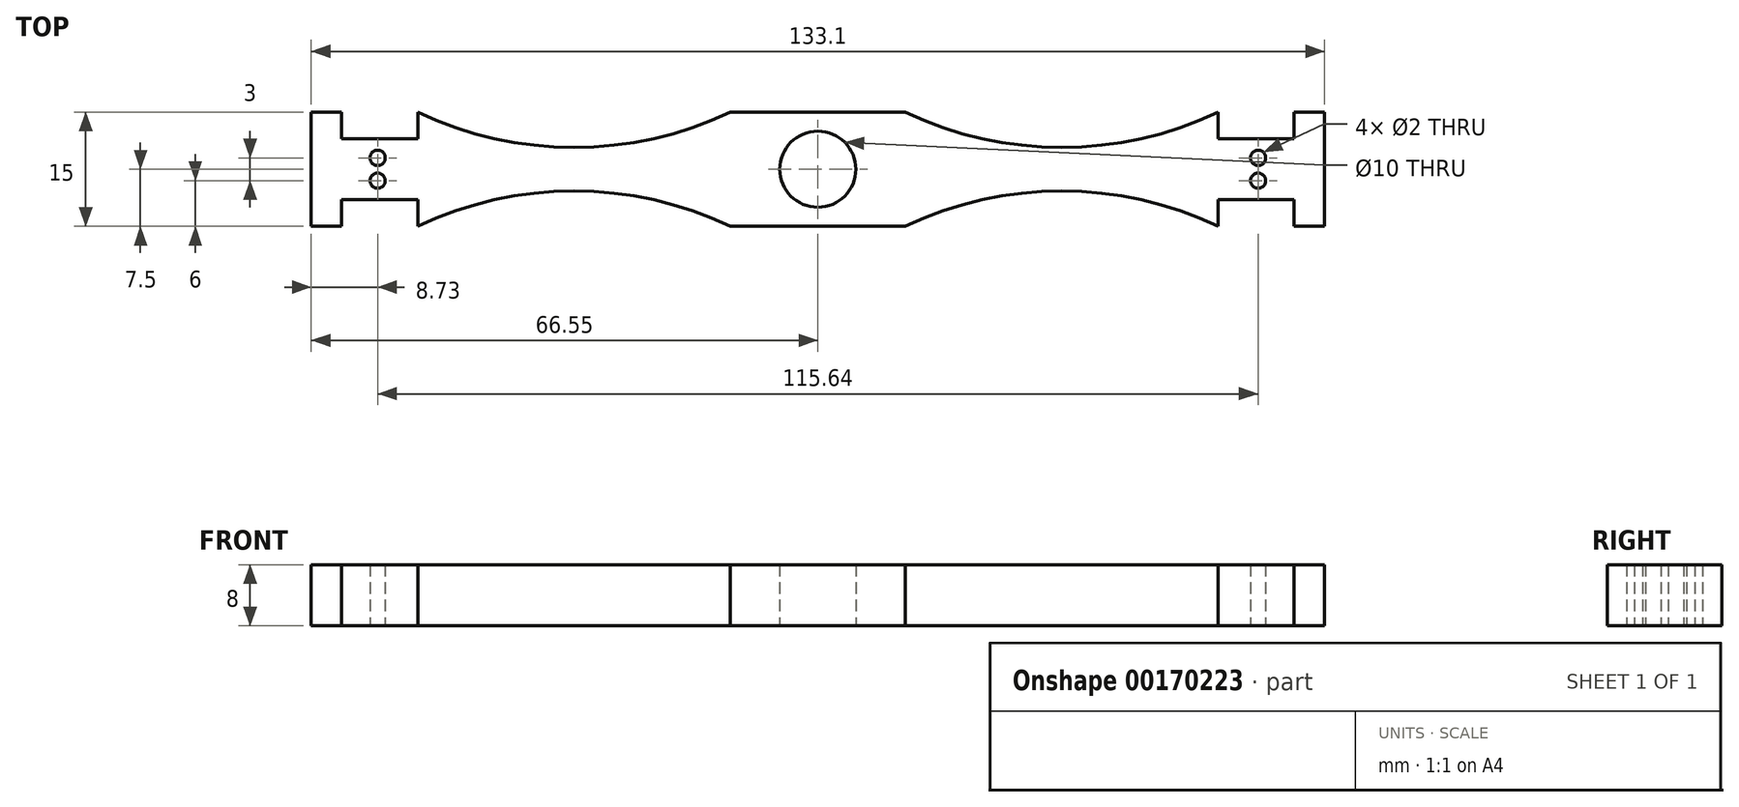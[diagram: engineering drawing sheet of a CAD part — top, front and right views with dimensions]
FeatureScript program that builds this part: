
annotation { "Feature Type Name" : "Feature", "Feature Type Description" : "" }
export const myFeature = defineFeature(function(context is Context, id is Id, definition is map)
    precondition{}
    {
        {
            var Q0;
            Q0=qCreatedBy(makeId("Top.planeOp"),FACE);
            var sketch = newSketch(context, id + "F0", { "sketchPlane" : qUnion([Q0])});
            skLineSegment(sketch, "E0.bottom", {"start": v(-11.5, 7.5) * mm, "end": v(11.5, 7.5) * mm});
            skLineSegment(sketch, "E0.top", {"start": v(-11.5, -7.5) * mm, "end": v(11.5, -7.5) * mm});
            skLineSegment(sketch, "E0.left", {"start": v(-11.5, 7.5) * mm, "end": v(-11.5, -7.5) * mm});
            skLineSegment(sketch, "E0.right", {"start": v(11.5, 7.5) * mm, "end": v(11.5, -7.5) * mm});
            skPoint(sketch, "E0.middle", {"position": v(0, 0) * mm});
            skArc(sketch, "E1", {"start": v(-52.55, 7.5) * mm, "mid": v(-32.02, 2.86) * mm, "end": v(-11.5, 7.5) * mm});
            skLineSegment(sketch, "E2", {"start": v(-52.55, 7.5) * mm, "end": v(-52.55, 4) * mm});
            skLineSegment(sketch, "E3", {"start": v(-52.55, 4) * mm, "end": v(-62.55, 4) * mm});
            skLineSegment(sketch, "E4", {"start": v(-62.55, 4) * mm, "end": v(-62.55, 7.5) * mm});
            skLineSegment(sketch, "E5", {"start": v(-62.55, 7.5) * mm, "end": v(-66.55, 7.5) * mm});
            skArc(sketch, "E6.MirrorCS", {"start": v(-52.55, -7.5) * mm, "mid": v(-32.02, -2.86) * mm, "end": v(-11.5, -7.5) * mm});
            skLineSegment(sketch, "E7.MirrorCS", {"start": v(-52.55, -4) * mm, "end": v(-62.55, -4) * mm});
            skLineSegment(sketch, "E8.MirrorCS", {"start": v(-62.55, -7.5) * mm, "end": v(-66.55, -7.5) * mm});
            skLineSegment(sketch, "E9.MirrorCS", {"start": v(-62.55, -4) * mm, "end": v(-62.55, -7.5) * mm});
            skLineSegment(sketch, "E10.MirrorCS", {"start": v(-52.55, -7.5) * mm, "end": v(-52.55, -4) * mm});
            skLineSegment(sketch, "E11", {"start": v(-66.55, 7.5) * mm, "end": v(-66.55, -7.5) * mm});
            skPoint(sketch, "E12", {"position": v(-57.82, 1.5) * mm});
            skPoint(sketch, "E13", {"position": v(-57.82, -1.5) * mm});
            skArc(sketch, "E14.MirrorCS", {"start": v(52.55, 7.5) * mm, "mid": v(32.02, 2.86) * mm, "end": v(11.5, 7.5) * mm});
            skArc(sketch, "E15.MirrorCS", {"start": v(52.55, -7.5) * mm, "mid": v(32.02, -2.86) * mm, "end": v(11.5, -7.5) * mm});
            skLineSegment(sketch, "E16.MirrorCS", {"start": v(52.55, 7.5) * mm, "end": v(52.55, 4) * mm});
            skLineSegment(sketch, "E17.MirrorCS", {"start": v(52.55, -7.5) * mm, "end": v(52.55, -4) * mm});
            skLineSegment(sketch, "E18.MirrorCS", {"start": v(52.55, -4) * mm, "end": v(62.55, -4) * mm});
            skLineSegment(sketch, "E19.MirrorCS", {"start": v(52.55, 4) * mm, "end": v(62.55, 4) * mm});
            skLineSegment(sketch, "E20.MirrorCS", {"start": v(62.55, 4) * mm, "end": v(62.55, 7.5) * mm});
            skLineSegment(sketch, "E21.MirrorCS", {"start": v(62.55, 7.5) * mm, "end": v(66.55, 7.5) * mm});
            skLineSegment(sketch, "E22.MirrorCS", {"start": v(66.55, 7.5) * mm, "end": v(66.55, -7.5) * mm});
            skLineSegment(sketch, "E23.MirrorCS", {"start": v(62.55, -7.5) * mm, "end": v(66.55, -7.5) * mm});
            skLineSegment(sketch, "E24.MirrorCS", {"start": v(62.55, -4) * mm, "end": v(62.55, -7.5) * mm});
            skPoint(sketch, "E25.MirrorP", {"position": v(57.82, -1.5) * mm});
            skPoint(sketch, "E26.MirrorP", {"position": v(57.82, 1.5) * mm});
            skSolve(sketch);
        }
        {
            var Q0;
            Q0 = qSketchRegion(id + "F0", true);
            extrude(context, id + "F1", {"entities" : qUnion([Q0]), "depth" : 8 * mm});
        }
        {
            var Q0;
            Q0=sQuery(id+"F0.wireOp",VERTEX,"E12");
            var Q1;
            Q1=sQuery(id+"F0.wireOp",VERTEX,"E13");
            var Q2;
            Q2=sQuery(id+"F0.wireOp",VERTEX,"E26.MirrorP");
            var Q3;
            Q3=sQuery(id+"F0.wireOp",VERTEX,"E25.MirrorP");
            var Q4;
            Q4=makeQuery(id+"F1.opExtrude","SWEPT_BODY",BODY,{"disambiguationData":[OSD([sQuery(id+"F0.wireOp",EDGE,"E0.bottom"),sQuery(id+"F0.wireOp",EDGE,"E0.top"),sQuery(id+"F0.wireOp",EDGE,"E1"),sQuery(id+"F0.wireOp",EDGE,"E2"),sQuery(id+"F0.wireOp",EDGE,"E3"),sQuery(id+"F0.wireOp",EDGE,"E4"),sQuery(id+"F0.wireOp",EDGE,"E5"),sQuery(id+"F0.wireOp",EDGE,"E6.MirrorCS"),sQuery(id+"F0.wireOp",EDGE,"E7.MirrorCS"),sQuery(id+"F0.wireOp",EDGE,"E8.MirrorCS"),sQuery(id+"F0.wireOp",EDGE,"E9.MirrorCS"),sQuery(id+"F0.wireOp",EDGE,"E10.MirrorCS"),sQuery(id+"F0.wireOp",EDGE,"E11"),sQuery(id+"F0.wireOp",EDGE,"E14.MirrorCS"),sQuery(id+"F0.wireOp",EDGE,"E15.MirrorCS"),sQuery(id+"F0.wireOp",EDGE,"E16.MirrorCS"),sQuery(id+"F0.wireOp",EDGE,"E17.MirrorCS"),sQuery(id+"F0.wireOp",EDGE,"E19.MirrorCS"),sQuery(id+"F0.wireOp",EDGE,"E20.MirrorCS"),sQuery(id+"F0.wireOp",EDGE,"E21.MirrorCS"),sQuery(id+"F0.wireOp",EDGE,"E22.MirrorCS"),sQuery(id+"F0.wireOp",EDGE,"E23.MirrorCS"),sQuery(id+"F0.wireOp",EDGE,"E24.MirrorCS"),sQuery(id+"F0.wireOp",EDGE,"E18.MirrorCS")])]});
            hole(context, id + "F2", {"style" : HoleStyle.SIMPLE, "endStyle" : HoleEndStyle.BLIND, "oppositeDirection" : true, "holeDiameter" : 2 * mm, "holeDepth" : 50 * mm, "startFromSketch" : true, "locations" : qUnion([Q0, Q1, Q2, Q3]), "scope" : qUnion([Q4])});
        }
        {
            var Q0;
            Q0=sQuery(id+"F0.wireOp",VERTEX,"E0.middle");
            var Q1;
            Q1=makeQuery(id+"F1.opExtrude","SWEPT_BODY",BODY,{"disambiguationData":[OSD([sQuery(id+"F0.wireOp",EDGE,"E0.bottom"),sQuery(id+"F0.wireOp",EDGE,"E0.top"),sQuery(id+"F0.wireOp",EDGE,"E1"),sQuery(id+"F0.wireOp",EDGE,"E2"),sQuery(id+"F0.wireOp",EDGE,"E3"),sQuery(id+"F0.wireOp",EDGE,"E4"),sQuery(id+"F0.wireOp",EDGE,"E5"),sQuery(id+"F0.wireOp",EDGE,"E6.MirrorCS"),sQuery(id+"F0.wireOp",EDGE,"E7.MirrorCS"),sQuery(id+"F0.wireOp",EDGE,"E8.MirrorCS"),sQuery(id+"F0.wireOp",EDGE,"E9.MirrorCS"),sQuery(id+"F0.wireOp",EDGE,"E10.MirrorCS"),sQuery(id+"F0.wireOp",EDGE,"E11"),sQuery(id+"F0.wireOp",EDGE,"E14.MirrorCS"),sQuery(id+"F0.wireOp",EDGE,"E15.MirrorCS"),sQuery(id+"F0.wireOp",EDGE,"E16.MirrorCS"),sQuery(id+"F0.wireOp",EDGE,"E17.MirrorCS"),sQuery(id+"F0.wireOp",EDGE,"E19.MirrorCS"),sQuery(id+"F0.wireOp",EDGE,"E20.MirrorCS"),sQuery(id+"F0.wireOp",EDGE,"E21.MirrorCS"),sQuery(id+"F0.wireOp",EDGE,"E22.MirrorCS"),sQuery(id+"F0.wireOp",EDGE,"E23.MirrorCS"),sQuery(id+"F0.wireOp",EDGE,"E24.MirrorCS"),sQuery(id+"F0.wireOp",EDGE,"E18.MirrorCS")])]});
            hole(context, id + "F3", {"style" : HoleStyle.SIMPLE, "endStyle" : HoleEndStyle.BLIND, "oppositeDirection" : true, "holeDiameter" : 10 * mm, "holeDepth" : 50 * mm, "startFromSketch" : true, "locations" : qUnion([Q0]), "scope" : qUnion([Q1])});
        }
    });
